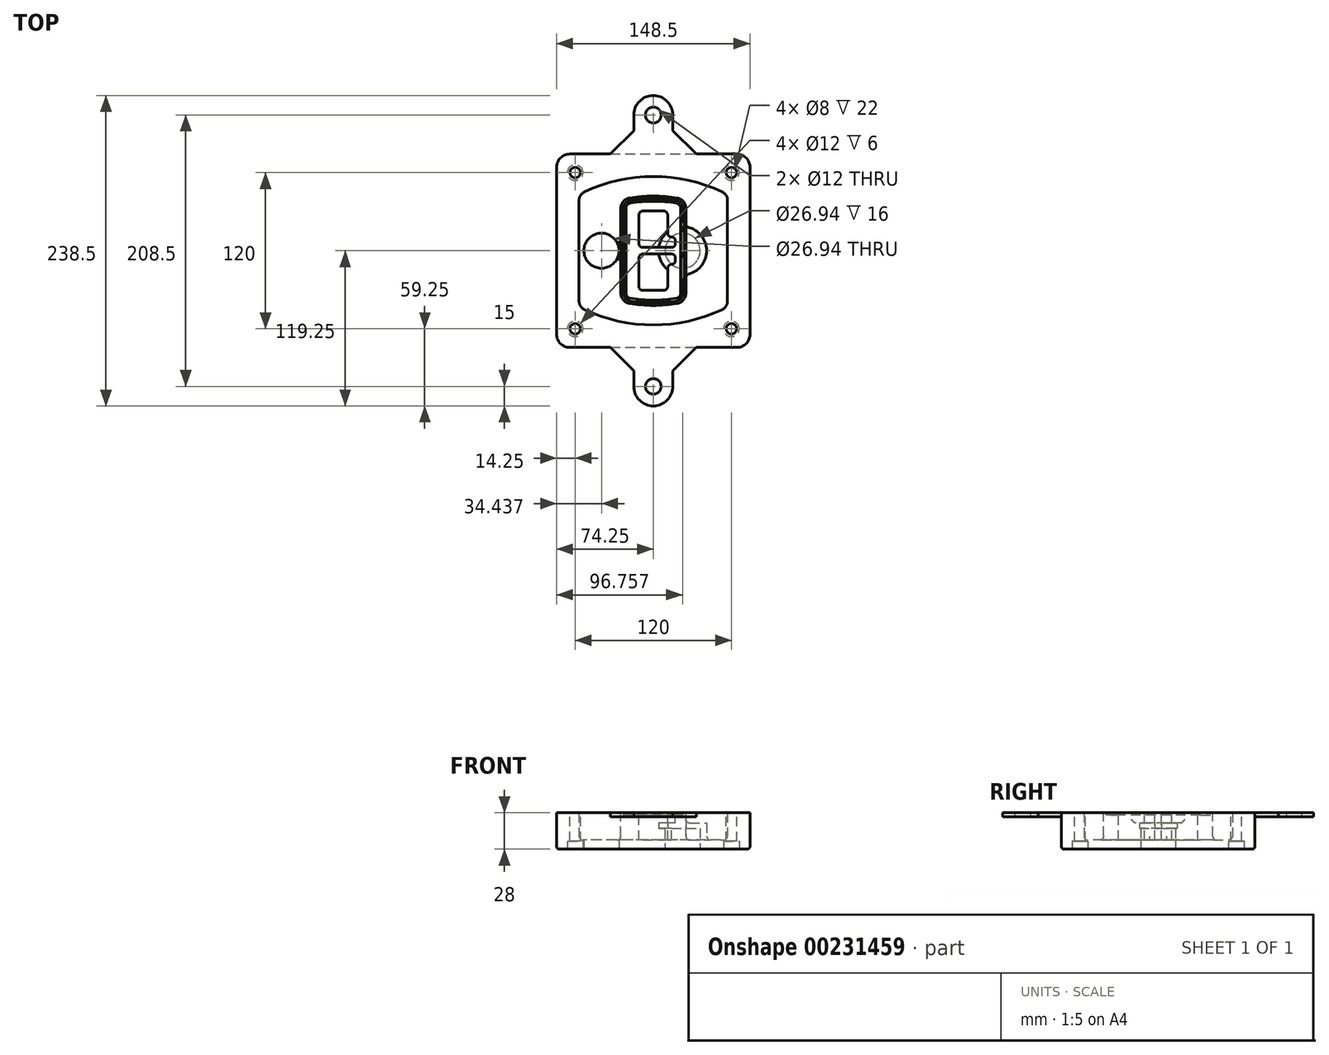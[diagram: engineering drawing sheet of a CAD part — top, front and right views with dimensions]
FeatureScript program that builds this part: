
annotation { "Feature Type Name" : "Feature", "Feature Type Description" : "" }
export const myFeature = defineFeature(function(context is Context, id is Id, definition is map)
    precondition{}
    {
        {
            var Q0;
            Q0=qCreatedBy(makeId("Top.planeOp"),FACE);
            var sketch = newSketch(context, id + "F0", { "sketchPlane" : qUnion([Q0])});
            skPoint(sketch, "E0.rect.middle", {"position": v(0, 0) * mm});
            skLineSegment(sketch, "E1.bottom", {"start": v(-64.25, -74.25) * mm, "end": v(64.25, -74.25) * mm});
            skLineSegment(sketch, "E1.top", {"start": v(-64.25, 74.25) * mm, "end": v(64.25, 74.25) * mm});
            skLineSegment(sketch, "E1.left", {"start": v(-74.25, -64.25) * mm, "end": v(-74.25, 64.25) * mm});
            skLineSegment(sketch, "E1.right", {"start": v(74.25, -64.25) * mm, "end": v(74.25, 64.25) * mm});
            skLineSegment(sketch, "E2", {"start": v(-74.25, 74.25) * mm, "end": v(74.25, -74.25) * mm, "construction": true});
            skLineSegment(sketch, "E3", {"start": v(74.25, 74.25) * mm, "end": v(-74.25, -74.25) * mm, "construction": true});
            skCircle(sketch, "E4", {"center": v(-60, 60) * mm, "radius": 4 * mm});
            skCircle(sketch, "E5", {"center": v(60, 60) * mm, "radius": 4 * mm});
            skCircle(sketch, "E6", {"center": v(60, -60) * mm, "radius": 4 * mm});
            skCircle(sketch, "E7", {"center": v(-60, -60) * mm, "radius": 4 * mm});
            skLineSegment(sketch, "E8", {"start": v(-60, 60) * mm, "end": v(60, 60) * mm, "construction": true});
            skLineSegment(sketch, "E9", {"start": v(60, 60) * mm, "end": v(60, -60) * mm, "construction": true});
            skLineSegment(sketch, "E10", {"start": v(60, -60) * mm, "end": v(-60, -60) * mm, "construction": true});
            skLineSegment(sketch, "E11", {"start": v(-60, -60) * mm, "end": v(-60, 60) * mm, "construction": true});
            skLineSegment(sketch, "E12", {"start": v(-60, 38.83) * mm, "end": v(-60, -38.83) * mm});
            skLineSegment(sketch, "E13", {"start": v(60, 38.83) * mm, "end": v(60, -38.83) * mm});
            skArc(sketch, "E14", {"start": v(54.26, 47.88) * mm, "mid": v(0, 60) * mm, "end": v(-54.26, 47.88) * mm});
            skArc(sketch, "E15", {"start": v(-54.26, -47.88) * mm, "mid": v(0, -60) * mm, "end": v(54.26, -47.88) * mm});
            skLineSegment(sketch, "E16", {"start": v(-60, 0) * mm, "end": v(60, 0) * mm, "construction": true});
            skPoint(sketch, "E17.visualSharp", {"position": v(-60, -45) * mm});
            skArc(sketch, "E17.filletArc", {"start": v(-60, -38.83) * mm, "mid": v(-58.44, -44.2) * mm, "end": v(-54.26, -47.88) * mm});
            skPoint(sketch, "E18.visualSharp", {"position": v(-60, 45) * mm});
            skArc(sketch, "E18.filletArc", {"start": v(-54.26, 47.88) * mm, "mid": v(-58.44, 44.2) * mm, "end": v(-60, 38.83) * mm});
            skPoint(sketch, "E19.visualSharp", {"position": v(60, 45) * mm});
            skArc(sketch, "E19.filletArc", {"start": v(60, 38.83) * mm, "mid": v(58.44, 44.2) * mm, "end": v(54.26, 47.88) * mm});
            skPoint(sketch, "E20.visualSharp", {"position": v(60, -45) * mm});
            skArc(sketch, "E20.filletArc", {"start": v(54.26, -47.88) * mm, "mid": v(58.44, -44.2) * mm, "end": v(60, -38.83) * mm});
            skPoint(sketch, "E21.visualSharp", {"position": v(-74.25, 74.25) * mm});
            skArc(sketch, "E21.filletArc", {"start": v(-64.25, 74.25) * mm, "mid": v(-71.32, 71.32) * mm, "end": v(-74.25, 64.25) * mm});
            skPoint(sketch, "E22.visualSharp", {"position": v(74.25, 74.25) * mm});
            skArc(sketch, "E22.filletArc", {"start": v(74.25, 64.25) * mm, "mid": v(71.32, 71.32) * mm, "end": v(64.25, 74.25) * mm});
            skPoint(sketch, "E23.visualSharp", {"position": v(74.25, -74.25) * mm});
            skArc(sketch, "E23.filletArc", {"start": v(64.25, -74.25) * mm, "mid": v(71.32, -71.32) * mm, "end": v(74.25, -64.25) * mm});
            skPoint(sketch, "E24.visualSharp", {"position": v(-74.25, -74.25) * mm});
            skArc(sketch, "E24.filletArc", {"start": v(-74.25, -64.25) * mm, "mid": v(-71.32, -71.32) * mm, "end": v(-64.25, -74.25) * mm});
            skArc(sketch, "E25.0", {"start": v(57, 38.83) * mm, "mid": v(55.9, 42.58) * mm, "end": v(52.98, 45.17) * mm});
            skLineSegment(sketch, "E25.1", {"start": v(57, 38.83) * mm, "end": v(57, -38.83) * mm});
            skArc(sketch, "E25.2", {"start": v(52.98, -45.17) * mm, "mid": v(55.9, -42.58) * mm, "end": v(57, -38.83) * mm});
            skArc(sketch, "E25.3", {"start": v(-52.98, -45.17) * mm, "mid": v(0, -57) * mm, "end": v(52.98, -45.17) * mm});
            skArc(sketch, "E25.4", {"start": v(-57, -38.83) * mm, "mid": v(-55.9, -42.58) * mm, "end": v(-52.98, -45.17) * mm});
            skArc(sketch, "E25.5", {"start": v(52.98, 45.17) * mm, "mid": v(0, 57) * mm, "end": v(-52.98, 45.17) * mm});
            skLineSegment(sketch, "E25.6", {"start": v(-57, 38.83) * mm, "end": v(-57, -38.83) * mm});
            skArc(sketch, "E25.7", {"start": v(-52.98, 45.17) * mm, "mid": v(-55.9, 42.58) * mm, "end": v(-57, 38.83) * mm});
            skArc(sketch, "E26.0", {"start": v(-55.96, 51.5) * mm, "mid": v(-61.82, 46.33) * mm, "end": v(-64, 38.83) * mm});
            skArc(sketch, "E26.1", {"start": v(55.96, 51.5) * mm, "mid": v(0, 64) * mm, "end": v(-55.96, 51.5) * mm});
            skArc(sketch, "E26.2", {"start": v(64, 38.83) * mm, "mid": v(61.82, 46.33) * mm, "end": v(55.96, 51.5) * mm});
            skLineSegment(sketch, "E26.3", {"start": v(64, 38.83) * mm, "end": v(64, -38.83) * mm});
            skArc(sketch, "E26.4", {"start": v(55.96, -51.5) * mm, "mid": v(61.82, -46.33) * mm, "end": v(64, -38.83) * mm});
            skLineSegment(sketch, "E26.5", {"start": v(-64, 38.83) * mm, "end": v(-64, -38.83) * mm});
            skArc(sketch, "E26.6", {"start": v(-55.96, -51.5) * mm, "mid": v(0, -64) * mm, "end": v(55.96, -51.5) * mm});
            skArc(sketch, "E26.7", {"start": v(-64, -38.83) * mm, "mid": v(-61.82, -46.33) * mm, "end": v(-55.96, -51.5) * mm});
            skSolve(sketch);
        }
        {
            var Q0;
            Q0=makeQuery(id+"F0.imprint","IMPRINT",FACE,{"disambiguationData":[TD([[makeQuery(id+"F0.imprint","IMPRINT",EDGE,{"derivedFrom":sQuery(id+"F0.wireOp",EDGE,"E1.bottom")}),1.0]])]});
            var Q1;
            Q1=makeQuery(id+"F0.imprint","IMPRINT",FACE,{"disambiguationData":[TD([[makeQuery(id+"F0.imprint","IMPRINT",EDGE,{"derivedFrom":sQuery(id+"F0.wireOp",EDGE,"E12")}),1.0]])]});
            var Q2;
            Q2=makeQuery(id+"F0.imprint","IMPRINT",FACE,{"disambiguationData":[TD([[makeQuery(id+"F0.imprint","IMPRINT",EDGE,{"derivedFrom":sQuery(id+"F0.wireOp",EDGE,"E25.0")}),1.0]])]});
            var Q3;
            Q3=makeQuery(id+"F0.imprint","IMPRINT",FACE,{"disambiguationData":[TD([[makeQuery(id+"F0.imprint","IMPRINT",EDGE,{"derivedFrom":sQuery(id+"F0.wireOp",EDGE,"E12")}),-1.0]])]});
            extrude(context, id + "F1", {"entities" : qUnion([Q0, Q1, Q2, Q3]), "oppositeDirection" : true, "depth" : 25 * mm});
        }
        {
            var Q0;
            Q0=makeQuery(id+"F0.imprint","IMPRINT",FACE,{"disambiguationData":[TD([[makeQuery(id+"F0.imprint","IMPRINT",EDGE,{"derivedFrom":sQuery(id+"F0.wireOp",EDGE,"E12")}),1.0]])]});
            extrude(context, id + "F2", {"entities" : qUnion([Q0]), "operationType" : NewBodyOperationType.ADD, "depth" : 3 * mm});
        }
        {
            var Q0;
            Q0=makeQuery(id+"F0.imprint","IMPRINT",FACE,{"disambiguationData":[TD([[makeQuery(id+"F0.imprint","IMPRINT",EDGE,{"derivedFrom":sQuery(id+"F0.wireOp",EDGE,"E25.0")}),1.0]])]});
            extrude(context, id + "F3", {"entities" : qUnion([Q0]), "operationType" : NewBodyOperationType.REMOVE, "oppositeDirection" : true, "depth" : 18 * mm});
        }
        {
            var Q0;
            Q0=makeQuery(id+"F2.opExtrude","CAP_FACE",FACE,{"disambiguationData":[OSD([sQuery(id+"F0.wireOp",EDGE,"E12"),sQuery(id+"F0.wireOp",EDGE,"E13"),sQuery(id+"F0.wireOp",EDGE,"E14"),sQuery(id+"F0.wireOp",EDGE,"E15"),sQuery(id+"F0.wireOp",EDGE,"E17.filletArc"),sQuery(id+"F0.wireOp",EDGE,"E18.filletArc"),sQuery(id+"F0.wireOp",EDGE,"E19.filletArc"),sQuery(id+"F0.wireOp",EDGE,"E20.filletArc"),sQuery(id+"F0.wireOp",EDGE,"E25.0"),sQuery(id+"F0.wireOp",EDGE,"E25.1"),sQuery(id+"F0.wireOp",EDGE,"E25.2"),sQuery(id+"F0.wireOp",EDGE,"E25.3"),sQuery(id+"F0.wireOp",EDGE,"E25.4"),sQuery(id+"F0.wireOp",EDGE,"E25.5"),sQuery(id+"F0.wireOp",EDGE,"E25.6"),sQuery(id+"F0.wireOp",EDGE,"E25.7")])],"isStart":false});
            var sketch = newSketch(context, id + "F4", { "sketchPlane" : qUnion([Q0])});
            skArc(sketch, "E27.0", {"start": v(-18.34, -40.45) * mm, "mid": v(0, -42) * mm, "end": v(18.34, -40.45) * mm});
            skArc(sketch, "E28.0", {"start": v(18.34, 40.45) * mm, "mid": v(0, 42) * mm, "end": v(-18.34, 40.45) * mm});
            skLineSegment(sketch, "E29", {"start": v(-25, 32.57) * mm, "end": v(-25, -32.57) * mm});
            skLineSegment(sketch, "E30", {"start": v(25, 32.57) * mm, "end": v(25, -32.57) * mm});
            skLineSegment(sketch, "E31", {"start": v(-25, 39.1) * mm, "end": v(25, 39.1) * mm, "construction": true});
            skLineSegment(sketch, "E32", {"start": v(-25, -39.1) * mm, "end": v(25, -39.1) * mm, "construction": true});
            skPoint(sketch, "E33.visualSharp", {"position": v(-25, 39.1) * mm});
            skArc(sketch, "E33.filletArc", {"start": v(-18.34, 40.45) * mm, "mid": v(-23.11, 37.73) * mm, "end": v(-25, 32.57) * mm});
            skPoint(sketch, "E34.visualSharp", {"position": v(25, 39.1) * mm});
            skArc(sketch, "E34.filletArc", {"start": v(25, 32.57) * mm, "mid": v(23.11, 37.73) * mm, "end": v(18.34, 40.45) * mm});
            skPoint(sketch, "E35.visualSharp", {"position": v(25, -39.1) * mm});
            skArc(sketch, "E35.filletArc", {"start": v(18.34, -40.45) * mm, "mid": v(23.11, -37.73) * mm, "end": v(25, -32.57) * mm});
            skPoint(sketch, "E36.visualSharp", {"position": v(-25, -39.1) * mm});
            skArc(sketch, "E36.filletArc", {"start": v(-25, -32.57) * mm, "mid": v(-23.11, -37.73) * mm, "end": v(-18.34, -40.45) * mm});
            skArc(sketch, "E37.0", {"start": v(52.98, 45.17) * mm, "mid": v(0, 57) * mm, "end": v(-52.98, 45.17) * mm});
            skArc(sketch, "E37.1", {"start": v(-52.98, 45.17) * mm, "mid": v(-55.9, 42.58) * mm, "end": v(-57, 38.83) * mm});
            skLineSegment(sketch, "E37.2", {"start": v(-57, 38.83) * mm, "end": v(-57, -38.83) * mm});
            skArc(sketch, "E37.3", {"start": v(-57, -38.83) * mm, "mid": v(-55.9, -42.58) * mm, "end": v(-52.98, -45.17) * mm});
            skArc(sketch, "E37.4", {"start": v(-52.98, -45.17) * mm, "mid": v(0, -57) * mm, "end": v(52.98, -45.17) * mm});
            skArc(sketch, "E37.5", {"start": v(52.98, -45.17) * mm, "mid": v(55.9, -42.58) * mm, "end": v(57, -38.83) * mm});
            skLineSegment(sketch, "E37.6", {"start": v(57, 38.83) * mm, "end": v(57, -38.83) * mm});
            skArc(sketch, "E37.7", {"start": v(57, 38.83) * mm, "mid": v(55.9, 42.58) * mm, "end": v(52.98, 45.17) * mm});
            skLineSegment(sketch, "E38.0", {"start": v(23, 32.57) * mm, "end": v(23, -32.57) * mm});
            skArc(sketch, "E38.1", {"start": v(18, -38.48) * mm, "mid": v(21.58, -36.44) * mm, "end": v(23, -32.57) * mm});
            skArc(sketch, "E38.2", {"start": v(-18, -38.48) * mm, "mid": v(0, -40) * mm, "end": v(18, -38.48) * mm});
            skArc(sketch, "E38.3", {"start": v(-23, -32.57) * mm, "mid": v(-21.58, -36.44) * mm, "end": v(-18, -38.48) * mm});
            skLineSegment(sketch, "E38.4", {"start": v(-23, 32.57) * mm, "end": v(-23, -32.57) * mm});
            skArc(sketch, "E38.5", {"start": v(23, 32.57) * mm, "mid": v(21.58, 36.44) * mm, "end": v(18, 38.48) * mm});
            skArc(sketch, "E38.6", {"start": v(-18, 38.48) * mm, "mid": v(-21.58, 36.44) * mm, "end": v(-23, 32.57) * mm});
            skArc(sketch, "E38.7", {"start": v(18, 38.48) * mm, "mid": v(0, 40) * mm, "end": v(-18, 38.48) * mm});
            skArc(sketch, "E39.0", {"start": v(21, 32.57) * mm, "mid": v(20.06, 35.15) * mm, "end": v(17.67, 36.5) * mm});
            skLineSegment(sketch, "E39.1", {"start": v(21, 32.57) * mm, "end": v(21, -32.57) * mm});
            skArc(sketch, "E39.2", {"start": v(17.67, -36.5) * mm, "mid": v(20.06, -35.15) * mm, "end": v(21, -32.57) * mm});
            skArc(sketch, "E39.3", {"start": v(-17.67, -36.5) * mm, "mid": v(0, -38) * mm, "end": v(17.67, -36.5) * mm});
            skArc(sketch, "E39.4", {"start": v(-21, -32.57) * mm, "mid": v(-20.06, -35.15) * mm, "end": v(-17.67, -36.5) * mm});
            skArc(sketch, "E39.5", {"start": v(17.67, 36.5) * mm, "mid": v(0, 38) * mm, "end": v(-17.67, 36.5) * mm});
            skLineSegment(sketch, "E39.6", {"start": v(-21, 32.57) * mm, "end": v(-21, -32.57) * mm});
            skArc(sketch, "E39.7", {"start": v(-17.67, 36.5) * mm, "mid": v(-20.06, 35.15) * mm, "end": v(-21, 32.57) * mm});
            skLineSegment(sketch, "E40", {"start": v(-25, 0) * mm, "end": v(25, 0) * mm, "construction": true});
            skLineSegment(sketch, "E41", {"start": v(-11, 5.5) * mm, "end": v(-11, 27.5) * mm});
            skLineSegment(sketch, "E42", {"start": v(-8, 30.5) * mm, "end": v(8, 30.5) * mm});
            skLineSegment(sketch, "E43", {"start": v(11, 27.5) * mm, "end": v(11, 13.5) * mm});
            skLineSegment(sketch, "E44", {"start": v(14, 10.5) * mm, "end": v(14, 10.5) * mm});
            skLineSegment(sketch, "E45", {"start": v(17, 7.5) * mm, "end": v(17, 5.5) * mm});
            skLineSegment(sketch, "E46", {"start": v(14, 2.5) * mm, "end": v(-8, 2.5) * mm});
            skPoint(sketch, "E47.visualSharp", {"position": v(-11, 30.5) * mm});
            skArc(sketch, "E47.filletArc", {"start": v(-8, 30.5) * mm, "mid": v(-10.12, 29.62) * mm, "end": v(-11, 27.5) * mm});
            skPoint(sketch, "E48.visualSharp", {"position": v(11, 30.5) * mm});
            skArc(sketch, "E48.filletArc", {"start": v(11, 27.5) * mm, "mid": v(10.12, 29.62) * mm, "end": v(8, 30.5) * mm});
            skPoint(sketch, "E49.visualSharp", {"position": v(11, 10.5) * mm});
            skArc(sketch, "E49.filletArc", {"start": v(11, 13.5) * mm, "mid": v(11.88, 11.38) * mm, "end": v(14, 10.5) * mm});
            skPoint(sketch, "E50.visualSharp", {"position": v(17, 10.5) * mm});
            skArc(sketch, "E50.filletArc", {"start": v(17, 7.5) * mm, "mid": v(16.12, 9.62) * mm, "end": v(14, 10.5) * mm});
            skPoint(sketch, "E51.visualSharp", {"position": v(17, 2.5) * mm});
            skArc(sketch, "E51.filletArc", {"start": v(14, 2.5) * mm, "mid": v(16.12, 3.38) * mm, "end": v(17, 5.5) * mm});
            skPoint(sketch, "E52.visualSharp", {"position": v(-11, 2.5) * mm});
            skArc(sketch, "E52.filletArc", {"start": v(-11, 5.5) * mm, "mid": v(-10.12, 3.38) * mm, "end": v(-8, 2.5) * mm});
            skLineSegment(sketch, "E53.0.MirrorCS", {"start": v(14, -2.5) * mm, "end": v(-8, -2.5) * mm});
            skArc(sketch, "E54.0.MirrorCS", {"start": v(-11, -5.5) * mm, "mid": v(-10.12, -3.38) * mm, "end": v(-8, -2.5) * mm});
            skLineSegment(sketch, "E55.0.MirrorCS", {"start": v(-11, -5.5) * mm, "end": v(-11, -27.5) * mm});
            skArc(sketch, "E56.0.MirrorCS", {"start": v(-8, -30.5) * mm, "mid": v(-10.12, -29.62) * mm, "end": v(-11, -27.5) * mm});
            skLineSegment(sketch, "E57.0.MirrorCS", {"start": v(-8, -30.5) * mm, "end": v(8, -30.5) * mm});
            skArc(sketch, "E58.0.MirrorCS", {"start": v(11, -27.5) * mm, "mid": v(10.12, -29.62) * mm, "end": v(8, -30.5) * mm});
            skLineSegment(sketch, "E59.0.MirrorCS", {"start": v(11, -27.5) * mm, "end": v(11, -13.5) * mm});
            skArc(sketch, "E60.0.MirrorCS", {"start": v(11, -13.5) * mm, "mid": v(11.88, -11.38) * mm, "end": v(14, -10.5) * mm});
            skArc(sketch, "E61.0.MirrorCS", {"start": v(17, -7.5) * mm, "mid": v(16.12, -9.62) * mm, "end": v(14, -10.5) * mm});
            skLineSegment(sketch, "E62.0.MirrorCS", {"start": v(17, -7.5) * mm, "end": v(17, -5.5) * mm});
            skArc(sketch, "E63.0.MirrorCS", {"start": v(14, -2.5) * mm, "mid": v(16.12, -3.38) * mm, "end": v(17, -5.5) * mm});
            skSolve(sketch);
        }
        {
            var Q0;
            Q0=makeQuery(id+"F4.imprint","IMPRINT",FACE,{"disambiguationData":[TD([[makeQuery(id+"F4.imprint","IMPRINT",EDGE,{"derivedFrom":sQuery(id+"F4.wireOp",EDGE,"E27.0")}),1.0]])]});
            var Q1;
            Q1=makeQuery(id+"F4.imprint","IMPRINT",FACE,{"disambiguationData":[TD([[makeQuery(id+"F4.imprint","IMPRINT",EDGE,{"derivedFrom":sQuery(id+"F4.wireOp",EDGE,"E38.0")}),-1.0]])]});
            var Q2;
            Q2=makeQuery(id+"F4.imprint","IMPRINT",FACE,{"disambiguationData":[TD([[makeQuery(id+"F4.imprint","IMPRINT",EDGE,{"derivedFrom":sQuery(id+"F4.wireOp",EDGE,"E39.0")}),1.0]])]});
            extrude(context, id + "F5", {"entities" : qUnion([Q0, Q1, Q2]), "operationType" : NewBodyOperationType.ADD, "endBound" : BoundingType.UP_TO_NEXT, "oppositeDirection" : true, "depth" : 25 * mm});
        }
        {
            var Q0;
            Q0=makeQuery(id+"F4.imprint","IMPRINT",FACE,{"disambiguationData":[TD([[makeQuery(id+"F4.imprint","IMPRINT",EDGE,{"derivedFrom":sQuery(id+"F4.wireOp",EDGE,"E38.0")}),-1.0]])]});
            extrude(context, id + "F6", {"entities" : qUnion([Q0]), "operationType" : NewBodyOperationType.REMOVE, "oppositeDirection" : true, "depth" : 2 * mm});
        }
        {
            var Q0;
            Q0=makeQuery(id+"F1.opExtrude","CAP_FACE",FACE,{"disambiguationData":[OSD([sQuery(id+"F0.wireOp",EDGE,"E1.bottom"),sQuery(id+"F0.wireOp",EDGE,"E1.top"),sQuery(id+"F0.wireOp",EDGE,"E1.left"),sQuery(id+"F0.wireOp",EDGE,"E1.right"),sQuery(id+"F0.wireOp",EDGE,"E4"),sQuery(id+"F0.wireOp",EDGE,"E5"),sQuery(id+"F0.wireOp",EDGE,"E6"),sQuery(id+"F0.wireOp",EDGE,"E7"),sQuery(id+"F0.wireOp",EDGE,"E21.filletArc"),sQuery(id+"F0.wireOp",EDGE,"E22.filletArc"),sQuery(id+"F0.wireOp",EDGE,"E23.filletArc"),sQuery(id+"F0.wireOp",EDGE,"E24.filletArc")])],"isStart":false});
            var sketch = newSketch(context, id + "F7", { "sketchPlane" : qUnion([Q0])});
            skCircle(sketch, "E64", {"center": v(22.5, 0) * mm, "radius": 13.47 * mm});
            skCircle(sketch, "E65", {"center": v(-39.81, 0) * mm, "radius": 13.47 * mm});
            skLineSegment(sketch, "E66", {"start": v(74.25, 0) * mm, "end": v(-74.25, 0) * mm});
            skCircle(sketch, "E67", {"center": v(22.5, 0) * mm, "radius": 18.47 * mm});
            skCircle(sketch, "E68", {"center": v(60, -60) * mm, "radius": 6 * mm});
            skCircle(sketch, "E69", {"center": v(-60, -60) * mm, "radius": 6 * mm});
            skCircle(sketch, "E70", {"center": v(-60, 60) * mm, "radius": 6 * mm});
            skCircle(sketch, "E71", {"center": v(60, 60) * mm, "radius": 6 * mm});
            skSolve(sketch);
        }
        {
            var Q0;
            {var subQ1=sQuery(id+"F7.wireOp",EDGE,"E66");var subQ4=sQuery(id+"F7.wireOp",EDGE,"E64");var subQ6=makeQuery(id+"F7.imprint","INTERSECT",VERTEX,{"disambiguationData":[OD(0.0)],"derivedFrom":[subQ4,subQ1]});Q0=makeQuery(id+"F7.imprint","IMPRINT",FACE,{"disambiguationData":[TD([[makeQuery(id+"F7.imprint","IMPRINT",EDGE,{"disambiguationData":[TD([[subQ6,-1.0]])],"derivedFrom":subQ4}),-1.0]])]});}
            var Q1;
            {var subQ0=sQuery(id+"F7.wireOp",EDGE,"E66");var subQ1=sQuery(id+"F7.wireOp",EDGE,"E64");var subQ3=makeQuery(id+"F7.imprint","INTERSECT",VERTEX,{"disambiguationData":[OD(0.0)],"derivedFrom":[subQ1,subQ0]});Q1=makeQuery(id+"F7.imprint","IMPRINT",FACE,{"disambiguationData":[TD([[makeQuery(id+"F7.imprint","IMPRINT",EDGE,{"disambiguationData":[TD([[subQ3,-1.0]])],"derivedFrom":subQ1}),1.0]])]});}
            var Q2;
            {var subQ0=sQuery(id+"F7.wireOp",EDGE,"E66");var subQ1=sQuery(id+"F7.wireOp",EDGE,"E64");var subQ3=makeQuery(id+"F7.imprint","INTERSECT",VERTEX,{"disambiguationData":[OD(0.0)],"derivedFrom":[subQ1,subQ0]});Q2=makeQuery(id+"F7.imprint","IMPRINT",FACE,{"disambiguationData":[TD([[makeQuery(id+"F7.imprint","IMPRINT",EDGE,{"disambiguationData":[TD([[subQ3,1.0]])],"derivedFrom":subQ1}),1.0]])]});}
            var Q3;
            {var subQ1=sQuery(id+"F7.wireOp",EDGE,"E66");var subQ4=sQuery(id+"F7.wireOp",EDGE,"E64");var subQ6=makeQuery(id+"F7.imprint","INTERSECT",VERTEX,{"disambiguationData":[OD(0.0)],"derivedFrom":[subQ4,subQ1]});Q3=makeQuery(id+"F7.imprint","IMPRINT",FACE,{"disambiguationData":[TD([[makeQuery(id+"F7.imprint","IMPRINT",EDGE,{"disambiguationData":[TD([[subQ6,1.0]])],"derivedFrom":subQ4}),-1.0]])]});}
            extrude(context, id + "F8", {"entities" : qUnion([Q0, Q1, Q2, Q3]), "operationType" : NewBodyOperationType.ADD, "oppositeDirection" : true, "depth" : 20 * mm});
        }
        {
            var Q0;
            {var subQ0=sQuery(id+"F7.wireOp",EDGE,"E66");var subQ1=sQuery(id+"F7.wireOp",EDGE,"E64");var subQ3=makeQuery(id+"F7.imprint","INTERSECT",VERTEX,{"disambiguationData":[OD(0.0)],"derivedFrom":[subQ1,subQ0]});Q0=makeQuery(id+"F7.imprint","IMPRINT",FACE,{"disambiguationData":[TD([[makeQuery(id+"F7.imprint","IMPRINT",EDGE,{"disambiguationData":[TD([[subQ3,-1.0]])],"derivedFrom":subQ1}),1.0]])]});}
            var Q1;
            {var subQ0=sQuery(id+"F7.wireOp",EDGE,"E66");var subQ1=sQuery(id+"F7.wireOp",EDGE,"E64");var subQ3=makeQuery(id+"F7.imprint","INTERSECT",VERTEX,{"disambiguationData":[OD(0.0)],"derivedFrom":[subQ1,subQ0]});Q1=makeQuery(id+"F7.imprint","IMPRINT",FACE,{"disambiguationData":[TD([[makeQuery(id+"F7.imprint","IMPRINT",EDGE,{"disambiguationData":[TD([[subQ3,1.0]])],"derivedFrom":subQ1}),1.0]])]});}
            extrude(context, id + "F9", {"entities" : qUnion([Q0, Q1]), "operationType" : NewBodyOperationType.REMOVE, "oppositeDirection" : true, "depth" : 16 * mm});
        }
        {
            var Q0;
            {var subQ0=sQuery(id+"F7.wireOp",EDGE,"E66");var subQ1=sQuery(id+"F7.wireOp",EDGE,"E65");var subQ3=makeQuery(id+"F7.imprint","INTERSECT",VERTEX,{"disambiguationData":[OD(0.0)],"derivedFrom":[subQ1,subQ0]});Q0=makeQuery(id+"F7.imprint","IMPRINT",FACE,{"disambiguationData":[TD([[makeQuery(id+"F7.imprint","IMPRINT",EDGE,{"disambiguationData":[TD([[subQ3,-1.0]])],"derivedFrom":subQ1}),1.0]])]});}
            var Q1;
            {var subQ0=sQuery(id+"F7.wireOp",EDGE,"E66");var subQ1=sQuery(id+"F7.wireOp",EDGE,"E65");var subQ3=makeQuery(id+"F7.imprint","INTERSECT",VERTEX,{"disambiguationData":[OD(0.0)],"derivedFrom":[subQ1,subQ0]});Q1=makeQuery(id+"F7.imprint","IMPRINT",FACE,{"disambiguationData":[TD([[makeQuery(id+"F7.imprint","IMPRINT",EDGE,{"disambiguationData":[TD([[subQ3,1.0]])],"derivedFrom":subQ1}),1.0]])]});}
            extrude(context, id + "F10", {"entities" : qUnion([Q0, Q1]), "operationType" : NewBodyOperationType.REMOVE, "oppositeDirection" : true, "depth" : 25 * mm});
        }
        {
            var Q0;
            Q0=makeQuery(id+"F7.imprint","IMPRINT",FACE,{"disambiguationData":[TD([[makeQuery(id+"F7.imprint","IMPRINT",EDGE,{"derivedFrom":sQuery(id+"F7.wireOp",EDGE,"E68")}),1.0]])]});
            var Q1;
            Q1=makeQuery(id+"F7.imprint","IMPRINT",FACE,{"disambiguationData":[TD([[makeQuery(id+"F7.imprint","IMPRINT",EDGE,{"derivedFrom":makeQuery(id+"F1.opExtrude","CAP_EDGE",EDGE,{"disambiguationData":[OSD([sQuery(id+"F0.wireOp",EDGE,"E5")])],"isStart":false})}),-1.0]])]});
            var Q2;
            Q2=makeQuery(id+"F7.imprint","IMPRINT",FACE,{"disambiguationData":[TD([[makeQuery(id+"F7.imprint","IMPRINT",EDGE,{"derivedFrom":sQuery(id+"F7.wireOp",EDGE,"E69")}),1.0]])]});
            var Q3;
            Q3=makeQuery(id+"F7.imprint","IMPRINT",FACE,{"disambiguationData":[TD([[makeQuery(id+"F7.imprint","IMPRINT",EDGE,{"derivedFrom":makeQuery(id+"F1.opExtrude","CAP_EDGE",EDGE,{"disambiguationData":[OSD([sQuery(id+"F0.wireOp",EDGE,"E4")])],"isStart":false})}),-1.0]])]});
            var Q4;
            Q4=makeQuery(id+"F7.imprint","IMPRINT",FACE,{"disambiguationData":[TD([[makeQuery(id+"F7.imprint","IMPRINT",EDGE,{"derivedFrom":sQuery(id+"F7.wireOp",EDGE,"E70")}),1.0]])]});
            var Q5;
            Q5=makeQuery(id+"F7.imprint","IMPRINT",FACE,{"disambiguationData":[TD([[makeQuery(id+"F7.imprint","IMPRINT",EDGE,{"derivedFrom":makeQuery(id+"F1.opExtrude","CAP_EDGE",EDGE,{"disambiguationData":[OSD([sQuery(id+"F0.wireOp",EDGE,"E7")])],"isStart":false})}),-1.0]])]});
            var Q6;
            Q6=makeQuery(id+"F7.imprint","IMPRINT",FACE,{"disambiguationData":[TD([[makeQuery(id+"F7.imprint","IMPRINT",EDGE,{"derivedFrom":sQuery(id+"F7.wireOp",EDGE,"E71")}),1.0]])]});
            var Q7;
            Q7=makeQuery(id+"F7.imprint","IMPRINT",FACE,{"disambiguationData":[TD([[makeQuery(id+"F7.imprint","IMPRINT",EDGE,{"derivedFrom":makeQuery(id+"F1.opExtrude","CAP_EDGE",EDGE,{"disambiguationData":[OSD([sQuery(id+"F0.wireOp",EDGE,"E6")])],"isStart":false})}),-1.0]])]});
            extrude(context, id + "F11", {"entities" : qUnion([Q0, Q1, Q2, Q3, Q4, Q5, Q6, Q7]), "operationType" : NewBodyOperationType.REMOVE, "oppositeDirection" : true, "depth" : 6 * mm});
        }
        {
            var Q0;
            Q0=makeQuery(id+"F9.boolean.opBoolean","COPY",FACE,{"derivedFrom":makeQuery(id+"F9.opExtrude","CAP_FACE",FACE,{"disambiguationData":[OSD([sQuery(id+"F7.wireOp",EDGE,"E64")])],"isStart":false})});
            var sketch = newSketch(context, id + "F12", { "sketchPlane" : qUnion([Q0])});
            skArc(sketch, "E72.0", {"start": v(11, 14.45) * mm, "mid": v(6.45, 9.13) * mm, "end": v(4.2, 2.5) * mm});
            skArc(sketch, "E72.1", {"start": v(4.2, -2.5) * mm, "mid": v(6.45, -9.13) * mm, "end": v(11, -14.45) * mm});
            skLineSegment(sketch, "E73", {"start": v(4.2, -2.5) * mm, "end": v(14, -2.5) * mm});
            skLineSegment(sketch, "E74.0", {"start": v(14, 2.5) * mm, "end": v(4.2, 2.5) * mm});
            skArc(sketch, "E74.1", {"start": v(14, 2.5) * mm, "mid": v(16.12, 3.38) * mm, "end": v(17, 5.5) * mm});
            skLineSegment(sketch, "E74.2", {"start": v(17, 7.5) * mm, "end": v(17, 5.5) * mm});
            skArc(sketch, "E74.3", {"start": v(17, 7.5) * mm, "mid": v(16.12, 9.62) * mm, "end": v(14, 10.5) * mm});
            skArc(sketch, "E74.4", {"start": v(11, 13.5) * mm, "mid": v(11.88, 11.38) * mm, "end": v(14, 10.5) * mm});
            skLineSegment(sketch, "E74.5", {"start": v(11, 14.45) * mm, "end": v(11, 13.5) * mm});
            skLineSegment(sketch, "E74.7", {"start": v(14, -2.5) * mm, "end": v(4.2, -2.5) * mm});
            skArc(sketch, "E74.8", {"start": v(14, -2.5) * mm, "mid": v(16.12, -3.38) * mm, "end": v(17, -5.5) * mm});
            skLineSegment(sketch, "E74.9", {"start": v(17, -7.5) * mm, "end": v(17, -5.5) * mm});
            skArc(sketch, "E74.10", {"start": v(17, -7.5) * mm, "mid": v(16.12, -9.62) * mm, "end": v(14, -10.5) * mm});
            skArc(sketch, "E74.11", {"start": v(11, -13.5) * mm, "mid": v(11.88, -11.38) * mm, "end": v(14, -10.5) * mm});
            skLineSegment(sketch, "E74.12", {"start": v(11, -14.45) * mm, "end": v(11, -13.5) * mm});
            skPoint(sketch, "E75.orphan", {"position": v(11, -27.5) * mm});
            skPoint(sketch, "E76.orphan", {"position": v(-8, -2.5) * mm});
            skPoint(sketch, "E77.orphan", {"position": v(-8, 2.5) * mm});
            skPoint(sketch, "E78.orphan", {"position": v(11, 27.5) * mm});
            skSolve(sketch);
        }
        {
            var Q0;
            {var subQ7=sQuery(id+"F12.wireOp",EDGE,"E72.0");var subQ14=sQuery(id+"F12.wireOp",EDGE,"E72.1");var subQ16=sQuery(id+"F12.wireOp",EDGE,"E74.1");var subQ18=sQuery(id+"F12.wireOp",EDGE,"E74.8");Q0=qUnion([makeQuery(id+"F12.imprint","IMPRINT",FACE,{"disambiguationData":[TD([[makeQuery(id+"F12.imprint","IMPRINT",EDGE,{"derivedFrom":subQ7}),1.0]])]}),makeQuery(id+"F12.imprint","IMPRINT",FACE,{"disambiguationData":[TD([[makeQuery(id+"F12.imprint","IMPRINT",EDGE,{"derivedFrom":subQ14}),1.0]])]}),makeQuery(id+"F12.imprint","IMPRINT",FACE,{"disambiguationData":[TD([[makeQuery(id+"F12.imprint","IMPRINT",EDGE,{"derivedFrom":subQ16}),1.0]])]}),makeQuery(id+"F12.imprint","IMPRINT",FACE,{"disambiguationData":[TD([[makeQuery(id+"F12.imprint","IMPRINT",EDGE,{"derivedFrom":subQ18}),-1.0]])]})]);}
            var Q1;
            Q1=makeQuery(id+"F5.boolean.opBoolean","SPLIT",FACE,{"disambiguationData":[TD([makeQuery(id+"F5.opExtrude","SWEPT_FACE",FACE,{"disambiguationData":[OSD([sQuery(id+"F4.wireOp",EDGE,"E41")])]})])],"derivedFrom":makeQuery(id+"F3.boolean.opBoolean","COPY",FACE,{"derivedFrom":makeQuery(id+"F3.opExtrude","CAP_FACE",FACE,{"disambiguationData":[OSD([sQuery(id+"F0.wireOp",EDGE,"E25.0"),sQuery(id+"F0.wireOp",EDGE,"E25.1"),sQuery(id+"F0.wireOp",EDGE,"E25.2"),sQuery(id+"F0.wireOp",EDGE,"E25.3"),sQuery(id+"F0.wireOp",EDGE,"E25.4"),sQuery(id+"F0.wireOp",EDGE,"E25.5"),sQuery(id+"F0.wireOp",EDGE,"E25.6"),sQuery(id+"F0.wireOp",EDGE,"E25.7")])],"isStart":false})})});
            extrude(context, id + "F13", {"entities" : qUnion([Q0]), "operationType" : NewBodyOperationType.REMOVE, "endBound" : BoundingType.UP_TO_SURFACE, "endBoundEntityFace" : qUnion([Q1]), "depth" : 25 * mm});
        }
        {
            var Q0;
            Q0=makeQuery(id+"F3.boolean.opBoolean","COPY",EDGE,{"derivedFrom":makeQuery(id+"F3.opExtrude","CAP_EDGE",EDGE,{"disambiguationData":[OSD([sQuery(id+"F0.wireOp",EDGE,"E25.6")])],"isStart":false})});
            var Q1;
            Q1=makeQuery(id+"F8.boolean.opBoolean","INTERSECT",EDGE,{"derivedFrom":[makeQuery(id+"F5.opExtrude","SWEPT_FACE",FACE,{"disambiguationData":[OSD([sQuery(id+"F4.wireOp",EDGE,"E30")])]}),makeQuery(id+"F8.opExtrude","CAP_FACE",FACE,{"disambiguationData":[OSD([sQuery(id+"F7.wireOp",EDGE,"E67")])],"isStart":false})]});
            var Q2;
            Q2=makeQuery(id+"F8.boolean.opBoolean","INTERSECT",EDGE,{"disambiguationData":[OD(1.0)],"derivedFrom":[makeQuery(id+"F5.opExtrude","SWEPT_FACE",FACE,{"disambiguationData":[OSD([sQuery(id+"F4.wireOp",EDGE,"E30")])]}),makeQuery(id+"F8.opExtrude","SWEPT_FACE",FACE,{"disambiguationData":[OSD([sQuery(id+"F7.wireOp",EDGE,"E67")])]})]});
            var Q3;
            {var subQ0=sQuery(id+"F4.wireOp",EDGE,"E30");Q3=makeQuery(id+"F8.boolean.opBoolean","SPLIT",EDGE,{"disambiguationData":[TD([makeQuery(id+"F5.opExtrude","SWEPT_FACE",FACE,{"disambiguationData":[OSD([sQuery(id+"F4.wireOp",EDGE,"E35.filletArc")])]})])],"derivedFrom":makeQuery(id+"F5.opExtrude","CAP_EDGE",EDGE,{"disambiguationData":[OSD([subQ0])],"isStart":false})});}
            var Q4;
            {var subQ0=sQuery(id+"F0.wireOp",EDGE,"E25.7");var subQ1=sQuery(id+"F0.wireOp",EDGE,"E25.1");var subQ2=sQuery(id+"F0.wireOp",EDGE,"E25.6");var subQ3=sQuery(id+"F0.wireOp",EDGE,"E25.5");var subQ4=sQuery(id+"F0.wireOp",EDGE,"E25.4");var subQ5=sQuery(id+"F0.wireOp",EDGE,"E25.0");var subQ6=sQuery(id+"F0.wireOp",EDGE,"E25.2");var subQ7=sQuery(id+"F0.wireOp",EDGE,"E25.3");Q4=makeQuery(id+"F8.boolean.opBoolean","INTERSECT",EDGE,{"derivedFrom":[makeQuery(id+"F5.boolean.opBoolean","SPLIT",FACE,{"disambiguationData":[TD([makeQuery(id+"F2.opExtrude","SWEPT_FACE",FACE,{"disambiguationData":[OSD([subQ5])]})])],"derivedFrom":makeQuery(id+"F3.boolean.opBoolean","COPY",FACE,{"derivedFrom":makeQuery(id+"F3.opExtrude","CAP_FACE",FACE,{"disambiguationData":[OSD([subQ5,subQ1,subQ6,subQ7,subQ4,subQ3,subQ2,subQ0])],"isStart":false})})}),makeQuery(id+"F8.opExtrude","SWEPT_FACE",FACE,{"disambiguationData":[OSD([sQuery(id+"F7.wireOp",EDGE,"E67")])]})]});}
            var Q5;
            Q5=makeQuery(id+"F8.boolean.opBoolean","INTERSECT",EDGE,{"disambiguationData":[OD(0.0)],"derivedFrom":[makeQuery(id+"F5.opExtrude","SWEPT_FACE",FACE,{"disambiguationData":[OSD([sQuery(id+"F4.wireOp",EDGE,"E30")])]}),makeQuery(id+"F8.opExtrude","SWEPT_FACE",FACE,{"disambiguationData":[OSD([sQuery(id+"F7.wireOp",EDGE,"E67")])]})]});
            fillet(context, id + "F14", {"entities" : qUnion([Q0, Q1, Q2, Q3, Q4, Q5]), "radius" : 3 * mm, "tangentPropagation" : true, "allowEdgeOverflow" : false});
        }
        {
            var Q0;
            Q0=makeQuery(id+"F1.opExtrude","CAP_EDGE",EDGE,{"disambiguationData":[OSD([sQuery(id+"F0.wireOp",EDGE,"E1.bottom")])],"isStart":false});
            fillet(context, id + "F15", {"entities" : qUnion([Q0]), "radius" : 2 * mm, "tangentPropagation" : true, "allowEdgeOverflow" : false});
        }
        {
            var Q0;
            {var subQ0=sQuery(id+"F0.wireOp",EDGE,"E22.filletArc");var subQ1=sQuery(id+"F0.wireOp",EDGE,"E7");var subQ2=sQuery(id+"F0.wireOp",EDGE,"E6");var subQ3=sQuery(id+"F0.wireOp",EDGE,"E5");var subQ4=sQuery(id+"F0.wireOp",EDGE,"E4");var subQ5=sQuery(id+"F0.wireOp",EDGE,"E1.bottom");var subQ6=sQuery(id+"F0.wireOp",EDGE,"E21.filletArc");var subQ7=sQuery(id+"F0.wireOp",EDGE,"E1.top");var subQ8=sQuery(id+"F0.wireOp",EDGE,"E1.left");var subQ9=sQuery(id+"F0.wireOp",EDGE,"E1.right");var subQ10=sQuery(id+"F0.wireOp",EDGE,"E23.filletArc");var subQ11=sQuery(id+"F0.wireOp",EDGE,"E24.filletArc");Q0=makeQuery(id+"F2.boolean.opBoolean","SPLIT",FACE,{"disambiguationData":[TD([makeQuery(id+"F1.opExtrude","SWEPT_FACE",FACE,{"disambiguationData":[OSD([subQ5])]})])],"derivedFrom":makeQuery(id+"F1.opExtrude","CAP_FACE",FACE,{"disambiguationData":[OSD([subQ5,subQ7,subQ8,subQ9,subQ4,subQ3,subQ2,subQ1,subQ6,subQ0,subQ10,subQ11])],"isStart":true})});}
            var sketch = newSketch(context, id + "F16", { "sketchPlane" : qUnion([Q0])});
            skLineSegment(sketch, "E79.0", {"start": v(-64.25, -74.25) * mm, "end": v(64.25, -74.25) * mm});
            skArc(sketch, "E79.1", {"start": v(-74.25, -64.25) * mm, "mid": v(-71.32, -71.32) * mm, "end": v(-64.25, -74.25) * mm});
            skLineSegment(sketch, "E79.2", {"start": v(-74.25, -64.25) * mm, "end": v(-74.25, 64.25) * mm});
            skArc(sketch, "E79.3", {"start": v(-64.25, 74.25) * mm, "mid": v(-71.32, 71.32) * mm, "end": v(-74.25, 64.25) * mm});
            skLineSegment(sketch, "E79.4", {"start": v(-64.25, 74.25) * mm, "end": v(64.25, 74.25) * mm});
            skArc(sketch, "E79.5", {"start": v(74.25, 64.25) * mm, "mid": v(71.32, 71.32) * mm, "end": v(64.25, 74.25) * mm});
            skLineSegment(sketch, "E79.6", {"start": v(74.25, -64.25) * mm, "end": v(74.25, 64.25) * mm});
            skArc(sketch, "E79.7", {"start": v(64.25, -74.25) * mm, "mid": v(71.32, -71.32) * mm, "end": v(74.25, -64.25) * mm});
            skArc(sketch, "E79.8", {"start": v(54.26, -47.88) * mm, "mid": v(58.44, -44.2) * mm, "end": v(60, -38.83) * mm});
            skArc(sketch, "E79.9", {"start": v(-60, -38.83) * mm, "mid": v(-58.44, -44.2) * mm, "end": v(-54.26, -47.88) * mm});
            skArc(sketch, "E79.10", {"start": v(-54.26, 47.88) * mm, "mid": v(-58.44, 44.2) * mm, "end": v(-60, 38.83) * mm});
            skArc(sketch, "E79.11", {"start": v(60, 38.83) * mm, "mid": v(58.44, 44.2) * mm, "end": v(54.26, 47.88) * mm});
            skArc(sketch, "E79.12", {"start": v(54.26, 47.88) * mm, "mid": v(0, 60) * mm, "end": v(-54.26, 47.88) * mm});
            skLineSegment(sketch, "E79.13", {"start": v(60, 38.83) * mm, "end": v(60, -38.83) * mm});
            skArc(sketch, "E79.14", {"start": v(-54.26, -47.88) * mm, "mid": v(0, -60) * mm, "end": v(54.26, -47.88) * mm});
            skLineSegment(sketch, "E79.15", {"start": v(-60, 38.83) * mm, "end": v(-60, -38.83) * mm});
            skCircle(sketch, "E79.16", {"center": v(-60, -60) * mm, "radius": 4 * mm});
            skLineSegment(sketch, "E80", {"start": v(-33, 74.25) * mm, "end": v(-15, 92.25) * mm});
            skLineSegment(sketch, "E81", {"start": v(-15, 92.25) * mm, "end": v(-15, 104.25) * mm});
            skLineSegment(sketch, "E82", {"start": v(33, 74.25) * mm, "end": v(15, 92.25) * mm});
            skLineSegment(sketch, "E83", {"start": v(15, 92.25) * mm, "end": v(15, 104.25) * mm});
            skLineSegment(sketch, "E84", {"start": v(0, 74.25) * mm, "end": v(0, 104.25) * mm});
            skCircle(sketch, "E85", {"center": v(0, 104.25) * mm, "radius": 6 * mm});
            skArc(sketch, "E86", {"start": v(15, 104.25) * mm, "mid": v(0, 119.25) * mm, "end": v(-15, 104.25) * mm});
            skLineSegment(sketch, "E87", {"start": v(-74.25, 0) * mm, "end": v(74.25, 0) * mm, "construction": true});
            skLineSegment(sketch, "E88.MirrorCS", {"start": v(33, -74.25) * mm, "end": v(15, -92.25) * mm});
            skLineSegment(sketch, "E89.MirrorCS", {"start": v(15, -92.25) * mm, "end": v(15, -104.25) * mm});
            skArc(sketch, "E90.MirrorCS", {"start": v(15, -104.25) * mm, "mid": v(0, -119.25) * mm, "end": v(-15, -104.25) * mm});
            skLineSegment(sketch, "E91.MirrorCS", {"start": v(-15, -92.25) * mm, "end": v(-15, -104.25) * mm});
            skLineSegment(sketch, "E92.MirrorCS", {"start": v(-33, -74.25) * mm, "end": v(-15, -92.25) * mm});
            skLineSegment(sketch, "E93.MirrorCS", {"start": v(0, -74.25) * mm, "end": v(0, -104.25) * mm});
            skCircle(sketch, "E94.MirrorC", {"center": v(0, -104.25) * mm, "radius": 6 * mm});
            skSolve(sketch);
        }
        {
            var Q0;
            {var subQ0=sQuery(id+"F16.wireOp",EDGE,"E80");Q0=makeQuery(id+"F16.imprint","IMPRINT",FACE,{"disambiguationData":[TD([[makeQuery(id+"F16.imprint","IMPRINT",EDGE,{"derivedFrom":subQ0}),-1.0]])]});}
            var Q1;
            {var subQ11=sQuery(id+"F16.wireOp",EDGE,"E79.1");Q1=makeQuery(id+"F16.imprint","IMPRINT",FACE,{"disambiguationData":[TD([[makeQuery(id+"F16.imprint","IMPRINT",EDGE,{"derivedFrom":subQ11}),1.0]])]});}
            var Q2;
            {var subQ0=sQuery(id+"F16.wireOp",EDGE,"E88.MirrorCS");Q2=makeQuery(id+"F16.imprint","IMPRINT",FACE,{"disambiguationData":[TD([[makeQuery(id+"F16.imprint","IMPRINT",EDGE,{"derivedFrom":subQ0}),-1.0]])]});}
            var Q3;
            Q3=makeQuery(id+"F2.opExtrude","CAP_FACE",FACE,{"disambiguationData":[OSD([sQuery(id+"F0.wireOp",EDGE,"E12"),sQuery(id+"F0.wireOp",EDGE,"E13"),sQuery(id+"F0.wireOp",EDGE,"E14"),sQuery(id+"F0.wireOp",EDGE,"E15"),sQuery(id+"F0.wireOp",EDGE,"E17.filletArc"),sQuery(id+"F0.wireOp",EDGE,"E18.filletArc"),sQuery(id+"F0.wireOp",EDGE,"E19.filletArc"),sQuery(id+"F0.wireOp",EDGE,"E20.filletArc"),sQuery(id+"F0.wireOp",EDGE,"E25.0"),sQuery(id+"F0.wireOp",EDGE,"E25.1"),sQuery(id+"F0.wireOp",EDGE,"E25.2"),sQuery(id+"F0.wireOp",EDGE,"E25.3"),sQuery(id+"F0.wireOp",EDGE,"E25.4"),sQuery(id+"F0.wireOp",EDGE,"E25.5"),sQuery(id+"F0.wireOp",EDGE,"E25.6"),sQuery(id+"F0.wireOp",EDGE,"E25.7")])],"isStart":false});
            extrude(context, id + "F17", {"entities" : qUnion([Q0, Q1, Q2]), "operationType" : NewBodyOperationType.ADD, "endBound" : BoundingType.UP_TO_SURFACE, "endBoundEntityFace" : qUnion([Q3]), "depth" : 25 * mm});
        }
    });
